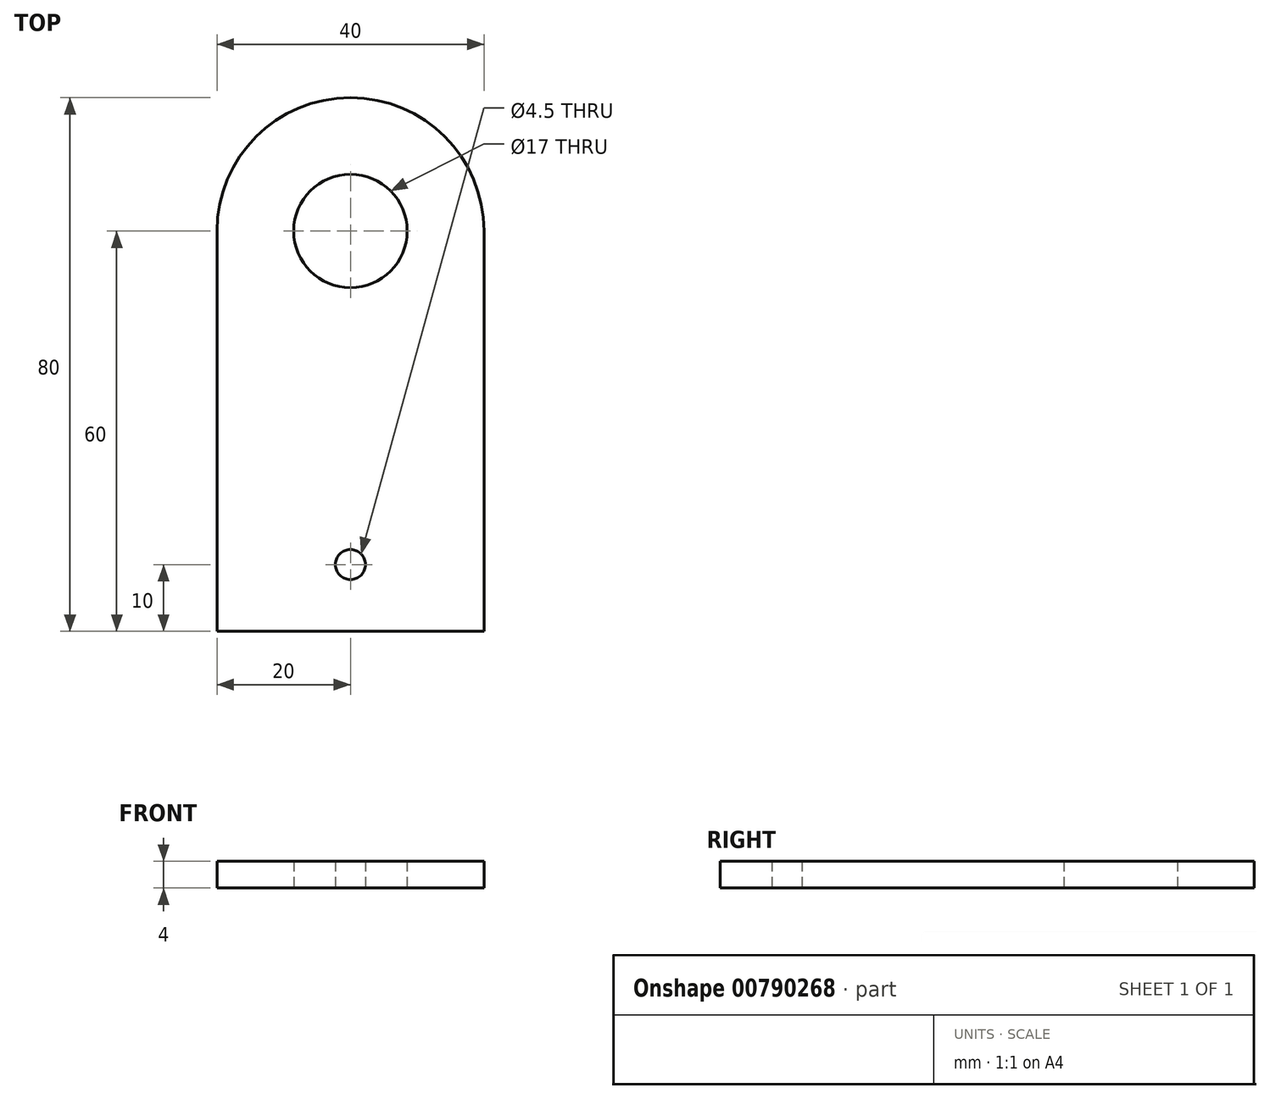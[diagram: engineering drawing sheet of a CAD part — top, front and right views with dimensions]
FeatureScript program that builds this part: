
annotation { "Feature Type Name" : "Feature", "Feature Type Description" : "" }
export const myFeature = defineFeature(function(context is Context, id is Id, definition is map)
    precondition{}
    {
        {
            var Q0;
            Q0=qCreatedBy(makeId("Top.planeOp"),FACE);
            var sketch = newSketch(context, id + "F0", { "sketchPlane" : qUnion([Q0])});
            skLineSegment(sketch, "E0.bottom", {"start": v(0, 0) * mm, "end": v(40, 0) * mm});
            skLineSegment(sketch, "E0.top", {"start": v(0, 80) * mm, "end": v(40, 80) * mm});
            skLineSegment(sketch, "E0.left", {"start": v(0, 0) * mm, "end": v(0, 80) * mm});
            skLineSegment(sketch, "E0.right", {"start": v(40, 0) * mm, "end": v(40, 80) * mm});
            skCircle(sketch, "E1", {"center": v(20, 60) * mm, "radius": 8.5 * mm});
            skCircle(sketch, "E2", {"center": v(20, 10) * mm, "radius": 2.25 * mm});
            skLineSegment(sketch, "E3", {"start": v(20, 80) * mm, "end": v(20, 0) * mm, "construction": true});
            skCircle(sketch, "E4", {"center": v(20, 60) * mm, "radius": 20 * mm});
            skSolve(sketch);
        }
        {
            var Q0;
            Q0=makeQuery(id+"F0.imprint","IMPRINT",FACE,{"disambiguationData":[TD([[makeQuery(id+"F0.imprint","IMPRINT",EDGE,{"derivedFrom":sQuery(id+"F0.wireOp",EDGE,"E0.bottom")}),1.0]])]});
            var Q1;
            Q1=makeQuery(id+"F0.imprint","IMPRINT",FACE,{"disambiguationData":[TD([[makeQuery(id+"F0.imprint","IMPRINT",EDGE,{"derivedFrom":sQuery(id+"F0.wireOp",EDGE,"E1")}),-1.0]])]});
            extrude(context, id + "F1", {"entities" : qUnion([Q0, Q1]), "depth" : 4 * mm, "offsetDistance" : 25 * mm});
        }
    });
